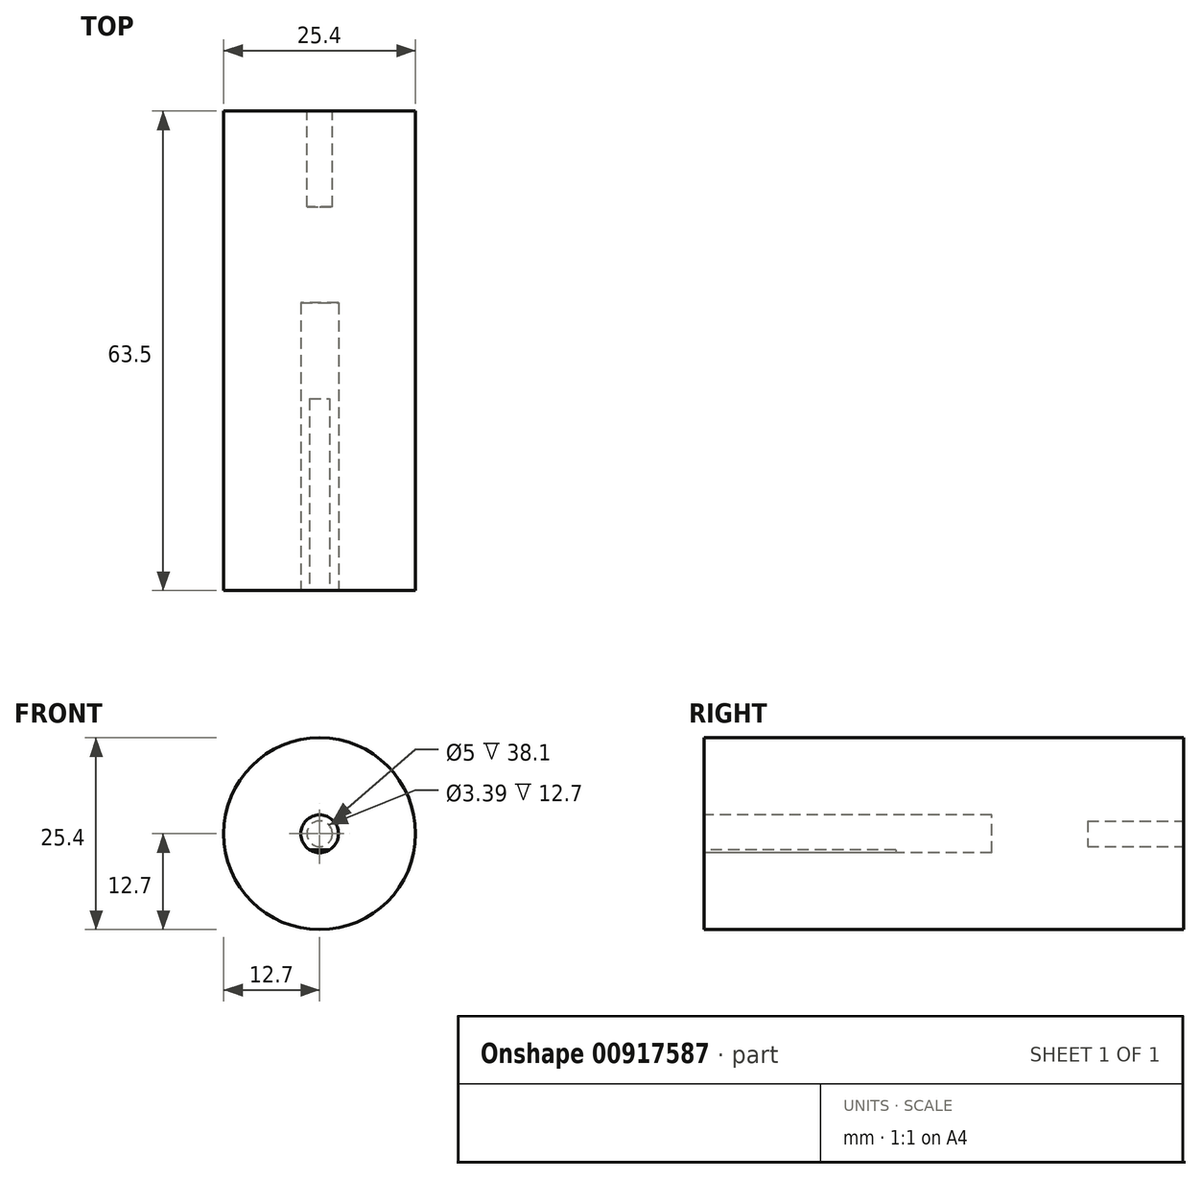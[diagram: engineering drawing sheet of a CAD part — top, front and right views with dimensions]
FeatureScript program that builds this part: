
annotation { "Feature Type Name" : "Feature", "Feature Type Description" : "" }
export const myFeature = defineFeature(function(context is Context, id is Id, definition is map)
    precondition{}
    {
        {
            var Q0;
            Q0=qCreatedBy(makeId("Front.planeOp"),FACE);
            var sketch = newSketch(context, id + "F0", { "sketchPlane" : qUnion([Q0])});
            skCircle(sketch, "E0", {"center": v(0, 0) * mm, "radius": 10.16 * mm});
            skSolve(sketch);
        }
        {
            var Q0;
            Q0 = qSketchRegion(id + "F0", true);
            extrude(context, id + "F1", {"entities" : qUnion([Q0]), "depth" : 50.8 * mm, "offsetDistance" : 25.4 * mm});
        }
        {
            var Q0;
            Q0=makeQuery(id+"F1.opExtrude","CAP_FACE",FACE,{"disambiguationData":[OSD([sQuery(id+"F0.wireOp",EDGE,"E0")])],"isStart":false});
            var sketch = newSketch(context, id + "F2", { "sketchPlane" : qUnion([Q0])});
            skCircle(sketch, "E1", {"center": v(0, 0) * mm, "radius": 0.25 * mm});
            skSolve(sketch);
        }
        {
            var Q0;
            Q0 = qSketchRegion(id + "F2", true);
            extrude(context, id + "F3", {"entities" : qUnion([Q0]), "operationType" : NewBodyOperationType.REMOVE, "oppositeDirection" : true, "depth" : 25.4 * mm, "offsetDistance" : 25.4 * mm});
        }
        {
            var Q0;
            Q0=makeQuery(id+"F1.opExtrude","SWEPT_BODY",BODY,{"disambiguationData":[OSD([sQuery(id+"F0.wireOp",EDGE,"E0")])]});
            deleteBodies(context, id + "F4", {"entities" : qUnion([Q0])});
        }
        {
            var Q0;
            Q0=qCreatedBy(makeId("Front.planeOp"),FACE);
            var sketch = newSketch(context, id + "F5", { "sketchPlane" : qUnion([Q0])});
            skCircle(sketch, "E2", {"center": v(0, 0) * mm, "radius": 12.7 * mm});
            skSolve(sketch);
        }
        {
            var Q0;
            Q0 = qSketchRegion(id + "F5", true);
            extrude(context, id + "F6", {"entities" : qUnion([Q0]), "endBound" : BoundingType.SYMMETRIC, "depth" : 63.5 * mm, "offsetDistance" : 25.4 * mm});
        }
        {
            var Q0;
            Q0=makeQuery(id+"F6.opExtrude","CAP_FACE",FACE,{"disambiguationData":[OSD([sQuery(id+"F5.wireOp",EDGE,"E2")])],"isStart":false});
            var sketch = newSketch(context, id + "F7", { "sketchPlane" : qUnion([Q0])});
            skCircle(sketch, "E3", {"center": v(0, 0) * mm, "radius": 2.5 * mm});
            skSolve(sketch);
        }
        {
            var Q0;
            Q0=makeQuery(id+"F7.imprint","IMPRINT",FACE,{"disambiguationData":[TD([[makeQuery(id+"F7.imprint","IMPRINT",EDGE,{"derivedFrom":sQuery(id+"F7.wireOp",EDGE,"E3")}),1.0]])]});
            extrude(context, id + "F8", {"entities" : qUnion([Q0]), "operationType" : NewBodyOperationType.REMOVE, "oppositeDirection" : true, "depth" : 38.1 * mm, "offsetDistance" : 25.4 * mm});
        }
        {
            var Q0;
            Q0=makeQuery(id+"F6.opExtrude","CAP_FACE",FACE,{"disambiguationData":[OSD([sQuery(id+"F5.wireOp",EDGE,"E2")])],"isStart":false});
            var sketch = newSketch(context, id + "F9", { "sketchPlane" : qUnion([Q0])});
            skLineSegment(sketch, "E4", {"start": v(0, -2.1) * mm, "end": v(-1.34, -2.1) * mm});
            skLineSegment(sketch, "E5", {"start": v(-1.34, -2.1) * mm, "end": v(1.34, -2.1) * mm});
            skSolve(sketch);
        }
        {
            var Q0;
            {var subQ0=sQuery(id+"F9.wireOp",EDGE,"E5");var subQ3=makeQuery(id+"F9.imprint","IMPRINT",VERTEX,{"derivedFrom":subQ0});Q0=makeQuery(id+"F9.imprint","IMPRINT",FACE,{"disambiguationData":[TD([[makeQuery(id+"F9.imprint","IMPRINT",EDGE,{"disambiguationData":[TD([[subQ3,1.0]])],"derivedFrom":subQ0}),-1.0]])]});}
            extrude(context, id + "F10", {"entities" : qUnion([Q0]), "oppositeDirection" : true, "depth" : 25.4 * mm, "offsetDistance" : 25.4 * mm});
        }
        {
            var Q0;
            Q0=makeQuery(id+"F6.opExtrude","CAP_FACE",FACE,{"disambiguationData":[OSD([sQuery(id+"F5.wireOp",EDGE,"E2")])],"isStart":true});
            var sketch = newSketch(context, id + "F11", { "sketchPlane" : qUnion([Q0])});
            skCircle(sketch, "E6", {"center": v(0, 0) * mm, "radius": 1.7 * mm});
            skSolve(sketch);
        }
        {
            var Q0;
            Q0 = qSketchRegion(id + "F11", true);
            extrude(context, id + "F12", {"entities" : qUnion([Q0]), "operationType" : NewBodyOperationType.REMOVE, "oppositeDirection" : true, "depth" : 12.7 * mm, "offsetDistance" : 25.4 * mm});
        }
    });
